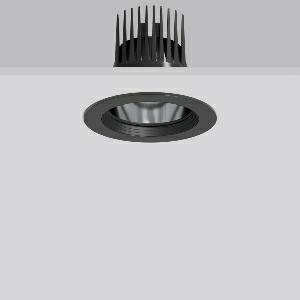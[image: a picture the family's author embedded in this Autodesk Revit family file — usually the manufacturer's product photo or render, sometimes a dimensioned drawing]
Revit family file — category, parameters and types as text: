
# Revit family: heledon_maxi_e_901758_003_76_e1da
name_source: partatom
category: Lighting Fixtures
units: mm (PartAtom-declared; Revit-internal decimal feet)

## family parameters
Cut with Voids When Loaded = No
Host = Face
Light Source = No
Part Type = Normal
Room Calculation Point = No
Round Connector Dimension = Use Diameter
Shared = No

## types (1)
- HELEDON maxi E (1 x LED Modul 930, 3350 lm, 3000)
    Apparent Load = 25 VA
    Approval mark = CE
    CIE Flux Codes = 100 100 100 100 100
    Color Rendering = 90
    Color Temperature = 3000
    Default Elevation = 1800 mm
    Description = Series: HELEDON maxi
Round recessed downlight. Housing: die-cast aluminium, powder-coated. Black plastic ring and recessed LED to prevent glare from the side. Optical assembly with reflector made of MIRO-Silver with 98% total light reflection for outstanding efficiency - can be changed without tools. Best colour rendering index Ra>90. Suitable for Recessed ceiling mounting. Installation without tools thanks to spring fastening system. Including separate LED converter with connecting cable 600 mm.High quality converter without flickering and stroboscopic effect. Through-wiring box (5 pole) available as accessory. The following accessories can be mounted without use of tools: interchangeable lenses, decorative glasses, honeycomb louvre, clear and frosted diffusers, white interchangeable plastic ring. 
Colour: deep black, matt (RAL 9005)
Diameter: 162 mm
Height: 3 mm
Cut-out diameter: 152 mm
Recess height: 200 mm
Luminaire: recess height: 135 mm
Lamp: LED
Socket: without socket
Colour temperature: 3000K
Colour rendering index (CRI): 92
System power: 25 W
Rated luminous flux: 3350 lm
Luminous efficiency: 134 lm/W
Control gear: Converter, dimmable, DALI
Protection class: II
Type of protection: IP 20
    Height = 0 mm  [stored 0 ft]
    Lamp = 1 x LED Modul 930
    Lamp Light Flux = 3350 lm
    Lamp count = 1
    Length = 162 mm
    Lifetime = 50000 h
    Luminous efficacy = 134 lm/W
    Manufacturer = RZB
    ModVariant = No
    Model = 901758.003.76
    Mounting Place = Ceiling
    Mounting Type = Recessed
    Number of Poles = 1
    OnlyDefault = Yes
    Power Factor = 1
    Product Name = HELEDON maxi E
    Product group = Recessed downlights
    ProductGroupID = 402
    Protection Class = Protection class II
    Protection Degree = IP 20
    RLX_Detail_Level = 1
    RLX_Emergency_Light_Flux = 0 lm
    RLX_Emergency_Type = 0
    RLX_Emergency_Type_DB = No
    RlxData = <blob elided: 122557 chars, md5=87260d38>
    Socket = socket
    Standby Power = 0 W
    System Light Flux = 3350 lm
    System Power = 25 W
    Type Comments = Product without accessories
    Type Image = 901662.003.jpg
    URL = http://relux.com
    VarID = ---
    Voltage = 230 V
    Voltage Range = 220-240 V
    Weight = 0.00 kg
    Width = 0 mm  [stored 0 ft]

note: [stored X ft] marks values corroborated as IEEE doubles in the binary element streams (Revit-internal decimal feet)

## geometry (parser evidence)
native form markers: Blend x4, Sweep x12
no freeform markers — native parametric forms only
